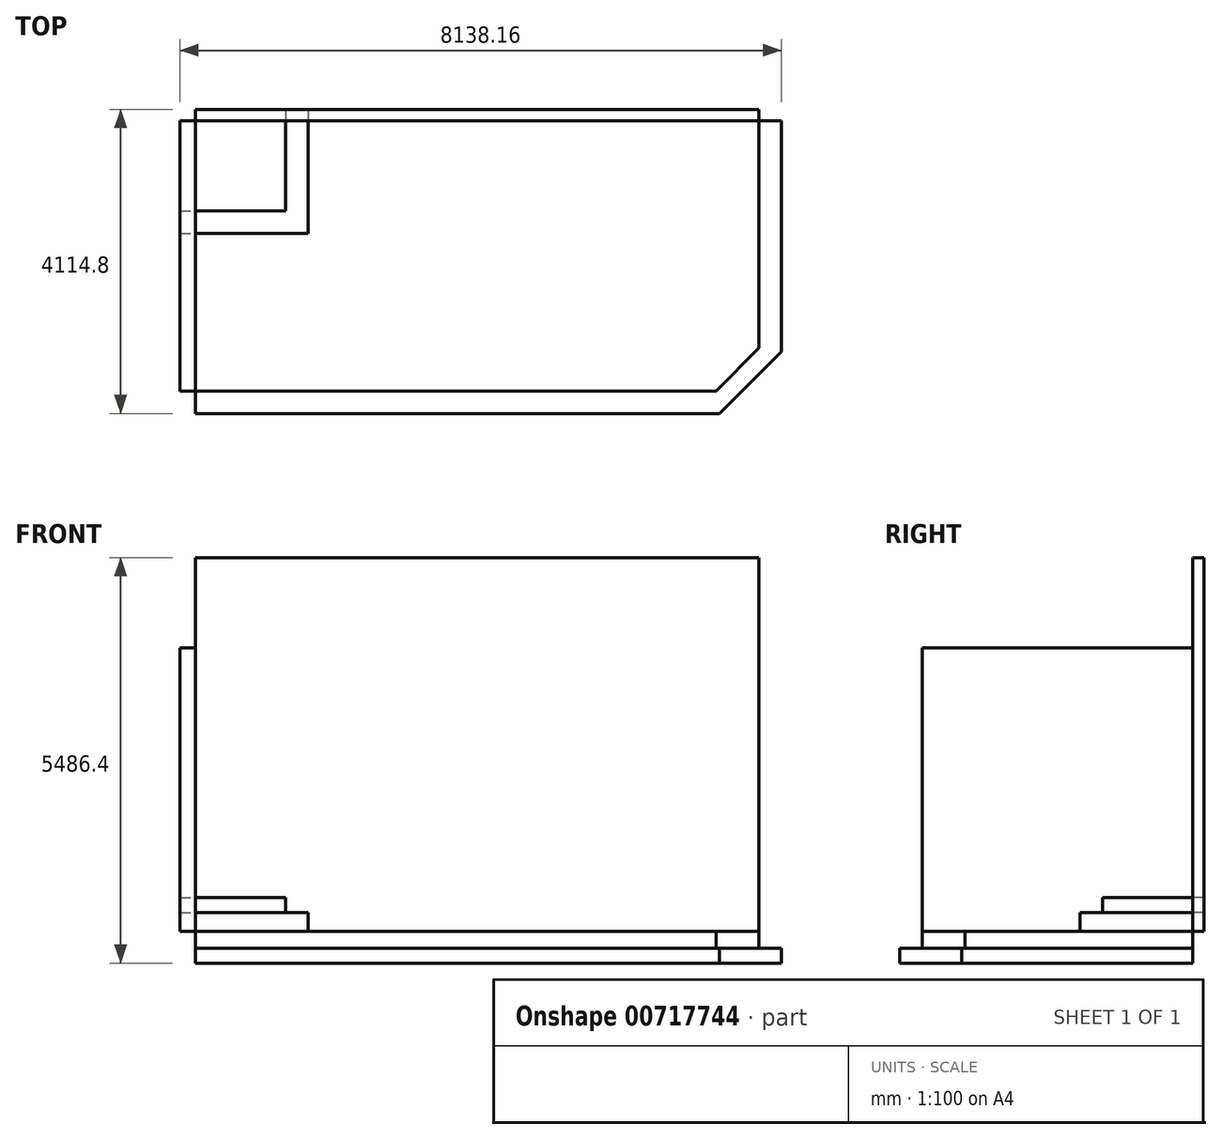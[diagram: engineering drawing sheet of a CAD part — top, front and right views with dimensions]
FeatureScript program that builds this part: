
annotation { "Feature Type Name" : "Feature", "Feature Type Description" : "" }
export const myFeature = defineFeature(function(context is Context, id is Id, definition is map)
    precondition{}
    {
        {
            var Q0;
            Q0=qCreatedBy(makeId("Top.planeOp"),FACE);
            var sketch = newSketch(context, id + "F0", { "sketchPlane" : qUnion([Q0])});
            skLineSegment(sketch, "E0.bottom", {"start": v(3810, -1828.8) * mm, "end": v(-3810, -1828.8) * mm});
            skLineSegment(sketch, "E0.top", {"start": v(3810, 1828.8) * mm, "end": v(-3810, 1828.8) * mm});
            skLineSegment(sketch, "E0.left", {"start": v(3810, -1828.8) * mm, "end": v(3810, 1828.8) * mm});
            skLineSegment(sketch, "E0.right", {"start": v(-3810, -1828.8) * mm, "end": v(-3810, 1828.8) * mm});
            skPoint(sketch, "E0.middle", {"position": v(0, 0) * mm});
            skSolve(sketch);
        }
        {
            var Q0;
            Q0=makeQuery(id+"F0.imprint","IMPRINT",FACE,{"disambiguationData":[TD([[makeQuery(id+"F0.imprint","IMPRINT",EDGE,{"derivedFrom":sQuery(id+"F0.wireOp",EDGE,"E0.bottom")}),-1.0]])]});
            extrude(context, id + "F1", {"entities" : qUnion([Q0]), "depth" : 426.72 * mm, "offsetDistance" : 30.48 * mm});
        }
        {
            var Q0;
            Q0=makeQuery(id+"F1.opExtrude","SWEPT_EDGE",EDGE,{"disambiguationData":[OSD([sQuery(id+"F0.wireOp",EDGE,"E0.bottom"),sQuery(id+"F0.wireOp",EDGE,"E0.left")])]});
            chamfer(context, id + "F2", {"entities" : qUnion([Q0]), "width" : 579.12 * mm, "tangentPropagation" : true});
        }
        {
            var Q0;
            Q0=makeQuery(id+"F1.opExtrude","CAP_FACE",FACE,{"disambiguationData":[OSD([sQuery(id+"F0.wireOp",EDGE,"E0.bottom"),sQuery(id+"F0.wireOp",EDGE,"E0.top"),sQuery(id+"F0.wireOp",EDGE,"E0.left"),sQuery(id+"F0.wireOp",EDGE,"E0.right")])],"isStart":true});
            var sketch = newSketch(context, id + "F3", { "sketchPlane" : qUnion([Q0])});
            skLineSegment(sketch, "E1.bottom", {"start": v(-3810, -1828.8) * mm, "end": v(4114.8, -1828.8) * mm});
            skLineSegment(sketch, "E1.top", {"start": v(-3810, 2133.6) * mm, "end": v(4114.8, 2133.6) * mm});
            skLineSegment(sketch, "E1.left", {"start": v(-3810, -1828.8) * mm, "end": v(-3810, 2133.6) * mm});
            skLineSegment(sketch, "E1.right", {"start": v(4114.8, -1828.8) * mm, "end": v(4114.8, 2133.6) * mm});
            skSolve(sketch);
        }
        {
            var Q0;
            {var subQ4=sQuery(id+"F3.wireOp",EDGE,"E1.top");Q0=makeQuery(id+"F3.imprint","IMPRINT",FACE,{"disambiguationData":[TD([[makeQuery(id+"F3.imprint","IMPRINT",EDGE,{"derivedFrom":subQ4}),-1.0]])]});}
            extrude(context, id + "F4", {"entities" : qUnion([Q0]), "operationType" : NewBodyOperationType.ADD, "oppositeDirection" : true, "depth" : 203.2 * mm, "offsetDistance" : 30.48 * mm});
        }
        {
            var Q0;
            Q0=makeQuery(id+"F4.opExtrude","SWEPT_EDGE",EDGE,{"disambiguationData":[OSD([sQuery(id+"F3.wireOp",EDGE,"E1.top"),sQuery(id+"F3.wireOp",EDGE,"E1.right")])]});
            chamfer(context, id + "F5", {"entities" : qUnion([Q0]), "width" : 838.2 * mm, "tangentPropagation" : true});
        }
        {
            var Q0;
            Q0=makeQuery(id+"F1.opExtrude","CAP_FACE",FACE,{"disambiguationData":[OSD([sQuery(id+"F0.wireOp",EDGE,"E0.bottom"),sQuery(id+"F0.wireOp",EDGE,"E0.top"),sQuery(id+"F0.wireOp",EDGE,"E0.left"),sQuery(id+"F0.wireOp",EDGE,"E0.right")])],"isStart":false});
            var sketch = newSketch(context, id + "F6", { "sketchPlane" : qUnion([Q0])});
            skLineSegment(sketch, "E2.bottom", {"start": v(-3810, 1828.8) * mm, "end": v(-2590.8, 1828.8) * mm});
            skLineSegment(sketch, "E2.top", {"start": v(-3810, 609.6) * mm, "end": v(-2590.8, 609.6) * mm});
            skLineSegment(sketch, "E2.left", {"start": v(-3810, 1828.8) * mm, "end": v(-3810, 609.6) * mm});
            skLineSegment(sketch, "E2.right", {"start": v(-2590.8, 1828.8) * mm, "end": v(-2590.8, 609.6) * mm});
            skSolve(sketch);
        }
        {
            var Q0;
            Q0=makeQuery(id+"F6.imprint","IMPRINT",FACE,{"disambiguationData":[TD([[makeQuery(id+"F6.imprint","IMPRINT",EDGE,{"derivedFrom":sQuery(id+"F6.wireOp",EDGE,"E2.bottom")}),1.0]])]});
            extrude(context, id + "F7", {"entities" : qUnion([Q0]), "operationType" : NewBodyOperationType.ADD, "depth" : 457.2 * mm, "offsetDistance" : 30.48 * mm});
        }
        {
            var Q0;
            {var subQ0=sQuery(id+"F0.wireOp",EDGE,"E0.right");var subQ1=sQuery(id+"F0.wireOp",EDGE,"E0.left");var subQ2=sQuery(id+"F0.wireOp",EDGE,"E0.top");var subQ3=sQuery(id+"F0.wireOp",EDGE,"E0.bottom");Q0=makeQuery(id+"F4.boolean.opBoolean","MERGE",FACE,{"derivedFrom":[makeQuery(id+"F1.opExtrude","CAP_FACE",FACE,{"disambiguationData":[OSD([subQ3,subQ2,subQ1,subQ0])],"isStart":true}),makeQuery(id+"F4.opExtrude","CAP_FACE",FACE,{"disambiguationData":[OSD([subQ3,subQ2,subQ1,subQ0,sQuery(id+"F3.wireOp",EDGE,"E1.bottom"),sQuery(id+"F3.wireOp",EDGE,"E1.top"),sQuery(id+"F3.wireOp",EDGE,"E1.left"),sQuery(id+"F3.wireOp",EDGE,"E1.right")])],"isStart":true})]});}
            var sketch = newSketch(context, id + "F8", { "sketchPlane" : qUnion([Q0])});
            skLineSegment(sketch, "E3.bottom", {"start": v(-3810, -1828.8) * mm, "end": v(-2286, -1828.8) * mm});
            skLineSegment(sketch, "E3.top", {"start": v(-3810, -304.8) * mm, "end": v(-2286, -304.8) * mm});
            skLineSegment(sketch, "E3.left", {"start": v(-3810, -1828.8) * mm, "end": v(-3810, -304.8) * mm});
            skLineSegment(sketch, "E3.right", {"start": v(-2286, -1828.8) * mm, "end": v(-2286, -304.8) * mm});
            skSolve(sketch);
        }
        {
            var Q0;
            Q0=makeQuery(id+"F8.imprint","IMPRINT",FACE,{"disambiguationData":[TD([[makeQuery(id+"F8.imprint","IMPRINT",EDGE,{"derivedFrom":sQuery(id+"F8.wireOp",EDGE,"E3.bottom")}),-1.0]])]});
            extrude(context, id + "F9", {"entities" : qUnion([Q0]), "operationType" : NewBodyOperationType.ADD, "oppositeDirection" : true, "depth" : 685.8 * mm, "offsetDistance" : 30.48 * mm});
        }
        {
            var Q0;
            Q0=makeQuery(id+"F9.boolean.opBoolean","MERGE",FACE,{"derivedFrom":[makeQuery(id+"F7.boolean.opBoolean","MERGE",FACE,{"derivedFrom":[makeQuery(id+"F4.boolean.opBoolean","MERGE",FACE,{"derivedFrom":[makeQuery(id+"F1.opExtrude","SWEPT_FACE",FACE,{"disambiguationData":[OSD([sQuery(id+"F0.wireOp",EDGE,"E0.top")])]}),makeQuery(id+"F4.opExtrude","SWEPT_FACE",FACE,{"disambiguationData":[OSD([sQuery(id+"F3.wireOp",EDGE,"E1.bottom")])]})]}),makeQuery(id+"F7.opExtrude","SWEPT_FACE",FACE,{"disambiguationData":[OSD([sQuery(id+"F6.wireOp",EDGE,"E2.bottom")])]})]}),makeQuery(id+"F9.opExtrude","SWEPT_FACE",FACE,{"disambiguationData":[OSD([sQuery(id+"F8.wireOp",EDGE,"E3.bottom")])]})]});
            var sketch = newSketch(context, id + "F10", { "sketchPlane" : qUnion([Q0])});
            skLineSegment(sketch, "E4.bottom", {"start": v(3810, 0) * mm, "end": v(-3810, 0) * mm});
            skLineSegment(sketch, "E4.top", {"start": v(3810, 5486.4) * mm, "end": v(-3810, 5486.4) * mm});
            skLineSegment(sketch, "E4.left", {"start": v(3810, 0) * mm, "end": v(3810, 5486.4) * mm});
            skLineSegment(sketch, "E4.right", {"start": v(-3810, 0) * mm, "end": v(-3810, 5486.4) * mm});
            skSolve(sketch);
        }
        {
            var Q0;
            {var subQ5=sQuery(id+"F10.wireOp",EDGE,"E4.top");Q0=makeQuery(id+"F10.imprint","IMPRINT",FACE,{"disambiguationData":[TD([[makeQuery(id+"F10.imprint","IMPRINT",EDGE,{"derivedFrom":subQ5}),1.0]])]});}
            extrude(context, id + "F11", {"entities" : qUnion([Q0]), "depth" : 152.4 * mm, "offsetDistance" : 30.48 * mm});
        }
        {
            var Q0;
            Q0=makeQuery(id+"F9.boolean.opBoolean","MERGE",FACE,{"derivedFrom":[makeQuery(id+"F7.boolean.opBoolean","MERGE",FACE,{"derivedFrom":[makeQuery(id+"F4.boolean.opBoolean","MERGE",FACE,{"derivedFrom":[makeQuery(id+"F1.opExtrude","SWEPT_FACE",FACE,{"disambiguationData":[OSD([sQuery(id+"F0.wireOp",EDGE,"E0.right")])]}),makeQuery(id+"F4.opExtrude","SWEPT_FACE",FACE,{"disambiguationData":[OSD([sQuery(id+"F3.wireOp",EDGE,"E1.left")])]})]}),makeQuery(id+"F7.opExtrude","SWEPT_FACE",FACE,{"disambiguationData":[OSD([sQuery(id+"F6.wireOp",EDGE,"E2.left")])]})]}),makeQuery(id+"F9.opExtrude","SWEPT_FACE",FACE,{"disambiguationData":[OSD([sQuery(id+"F8.wireOp",EDGE,"E3.left")])]})]});
            var sketch = newSketch(context, id + "F12", { "sketchPlane" : qUnion([Q0])});
            skLineSegment(sketch, "E5.bottom", {"start": v(-1828.8, 0) * mm, "end": v(1828.8, 0) * mm});
            skLineSegment(sketch, "E5.top", {"start": v(-1828.8, 4267.2) * mm, "end": v(1828.8, 4267.2) * mm});
            skLineSegment(sketch, "E5.left", {"start": v(-1828.8, 0) * mm, "end": v(-1828.8, 4267.2) * mm});
            skLineSegment(sketch, "E5.right", {"start": v(1828.8, 0) * mm, "end": v(1828.8, 4267.2) * mm});
            skSolve(sketch);
        }
        {
            var Q0;
            {var subQ5=sQuery(id+"F12.wireOp",EDGE,"E5.top");Q0=makeQuery(id+"F12.imprint","IMPRINT",FACE,{"disambiguationData":[TD([[makeQuery(id+"F12.imprint","IMPRINT",EDGE,{"derivedFrom":subQ5}),-1.0]])]});}
            extrude(context, id + "F13", {"entities" : qUnion([Q0]), "depth" : 213.36 * mm, "offsetDistance" : 30.48 * mm});
        }
    });
